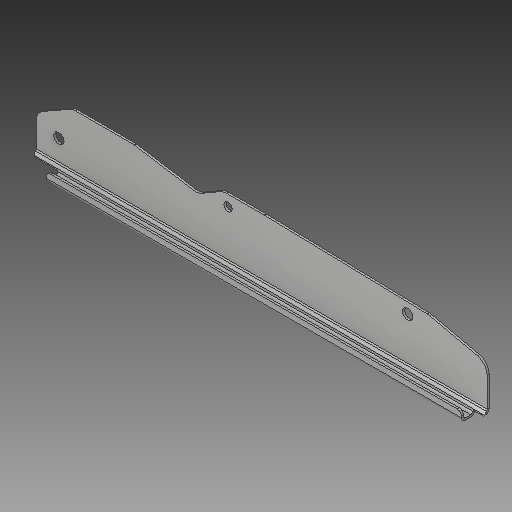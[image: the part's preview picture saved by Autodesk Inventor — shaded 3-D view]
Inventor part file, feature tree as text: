
AUTODESK INVENTOR PART (.ipt)
format: ipt  version: 2019 (Build 230136000, 136)  size: 274,944 bytes
history: native  units: mm
features: sketch x5, sheet_metal_op x4, fillet x3, extrude x2, hole x2, other x2, projected_geometry x2
ambient origin geometry x8: Origin, YZ Plane, XZ Plane, XY Plane, X Axis, Y Axis, Z Axis, Center Point
bodies: Solid1 (feature_tree)
feature tree (20):
  sheet_metal_op  "Face1"
  sheet_metal_op  "Contour Flange1"
  extrude  "Extrusion1"  Depth=2.0mm
  extrude  "Extrusion2"  Depth=2.0mm
  fillet  "Fillet1"  Radius=1.0mm
  fillet  "Fillet2"  Radius=4.0mm
  fillet  "Fillet3"  Radius=2.0mm
  sketch  "Sketch5"  dims[d39=2.0mm d42=23.0mm d43=0.0mm d44=12.0mm d45=0.0mm d46=12.0mm d47=4.0mm d48=2.0mm d65=22.0mm d68=186.0mm d70=360.0mm d72=10.0mm d73=6.0mm d74=4.0mm d75=2.0mm d76=90.0deg d77=2.0mm d78=20.594885mm d79=8.15mm d80=6.0mm d81=4.0mm d82=2.0mm d83=90.0deg d84=2.0mm d85=20.594885mm d86=2.0mm d87=2.0mm d88=4.0mm d90=4.0mm d91=0.666667mm d92=2.0mm d93=2.25mm d94=5.0mm d95=5.6mm d96=52.0mm d97=30.5mm d98=55.0mm]
  hole  "Hole1"  [1 undecoded]
  hole  "Hole2"  [1 undecoded]
  sketch  "Sketch1"  dims[d0=50.842275mm d1=31.0mm d2=35.0mm d3=59.0mm d4=1.570796mm d5=4.0mm d6=40.0mm d7=38.0mm d8=57.0mm d9=437.0mm d10=63.0mm d11=24.0mm d12=2.0mm]
  other  "Plate1"
  sketch  "Sketch2"  dims[d13=50.9mm d31=2.0mm d32=1.0mm d33=4.0mm d34=2.0mm]
  other  "Plate2"
  sheet_metal_op  "Bend1"
  sheet_metal_op  "Corner1"
  sketch  "Sketch3"  dims[d35=2.0mm d36=2.0mm]
  sketch  "Sketch4"  dims[d37=8.0mm d38=2.0mm]
  projected_geometry  "Projected Loop6"
  projected_geometry  "Projected Loop7"
note: 2 required parameter values undecoded (feature->parameter linkage not recoverable at this tier; creation-order binding heuristic only, values carry confidence <= 0.55)
